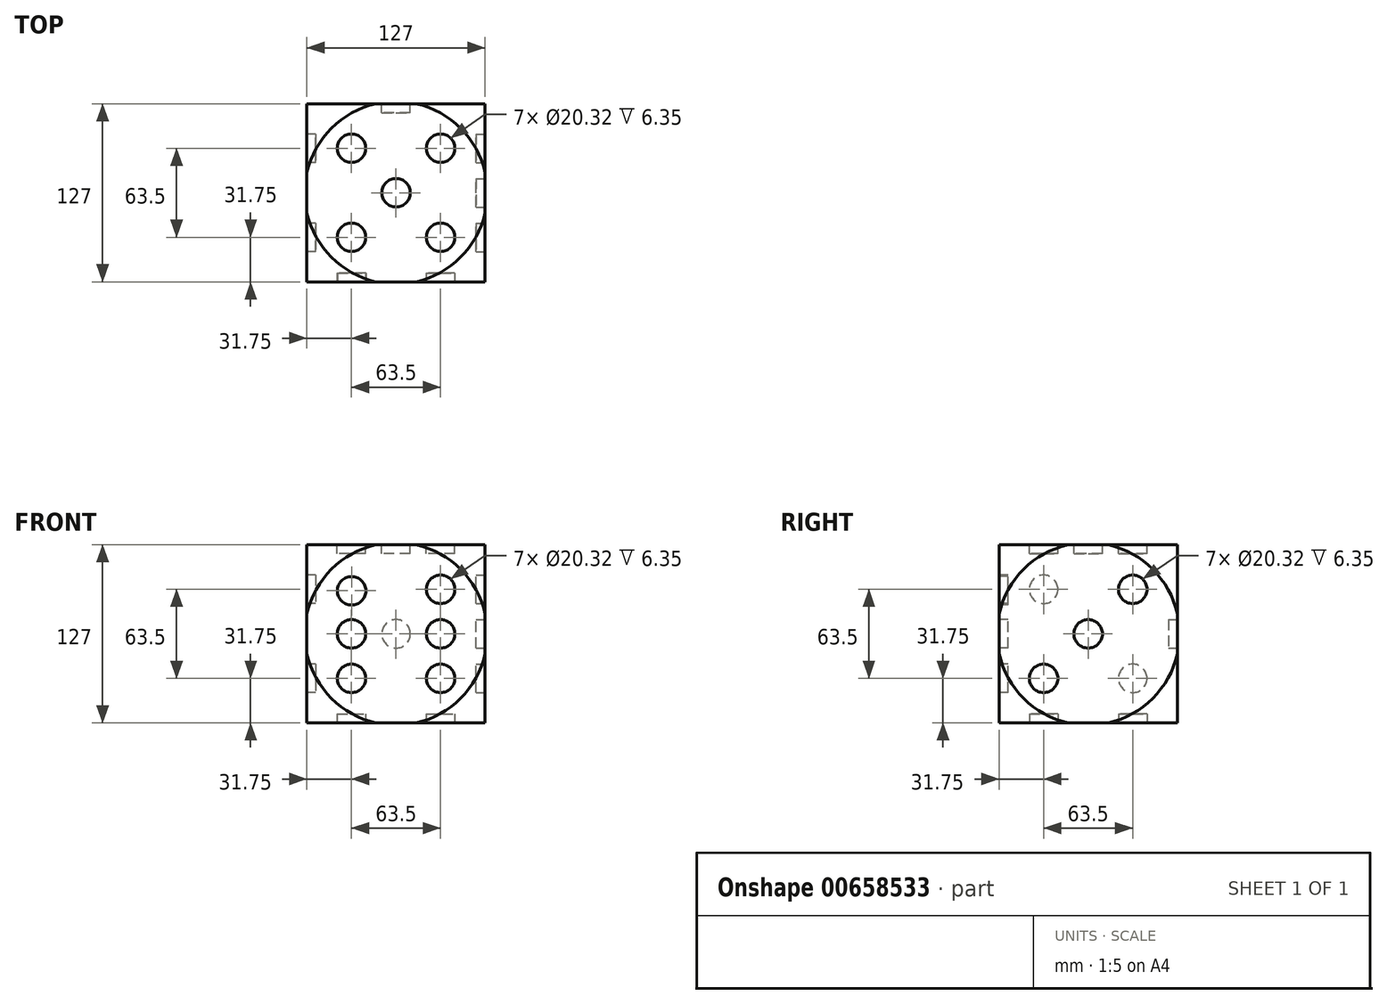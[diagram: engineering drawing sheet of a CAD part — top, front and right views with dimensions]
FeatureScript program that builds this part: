
annotation { "Feature Type Name" : "Feature", "Feature Type Description" : "" }
export const myFeature = defineFeature(function(context is Context, id is Id, definition is map)
    precondition{}
    {
        {
            var Q0;
            Q0=qCreatedBy(makeId("Top.planeOp"),FACE);
            var sketch = newSketch(context, id + "F0", { "sketchPlane" : qUnion([Q0])});
            skLineSegment(sketch, "E0.bottom", {"start": v(63.5, -63.5) * mm, "end": v(-63.5, -63.5) * mm});
            skLineSegment(sketch, "E0.top", {"start": v(63.5, 63.5) * mm, "end": v(-63.5, 63.5) * mm});
            skLineSegment(sketch, "E0.left", {"start": v(63.5, -63.5) * mm, "end": v(63.5, 63.5) * mm});
            skLineSegment(sketch, "E0.right", {"start": v(-63.5, -63.5) * mm, "end": v(-63.5, 63.5) * mm});
            skPoint(sketch, "E0.middle", {"position": v(0, 0) * mm});
            skSolve(sketch);
        }
        {
            var Q0;
            Q0=qCreatedBy(makeId("Top.planeOp"),FACE);
            cPlane(context, id + "F1", {"entities" : qUnion([Q0]), "cplaneType" : CPlaneType.OFFSET, "offset" : 63.5 * mm, "width" : 152.4 * mm, "height" : 152.4 * mm});
        }
        {
            var Q0;
            Q0 = qSketchRegion(id + "F0", true);
            extrude(context, id + "F2", {"entities" : qUnion([Q0]), "depth" : 127 * mm, "offsetDistance" : 25.4 * mm});
        }
        {
            var Q0;
            Q0=qCreatedBy(id+"F1.planeOp",FACE);
            var sketch = newSketch(context, id + "F3", { "sketchPlane" : qUnion([Q0])});
            skArc(sketch, "E1", {"start": v(0, 90.94) * mm, "mid": v(-90.94, 0) * mm, "end": v(0, -90.94) * mm});
            skLineSegment(sketch, "E2", {"start": v(0, 90.94) * mm, "end": v(0, -90.94) * mm});
            skSolve(sketch);
        }
        {
            var Q0;
            Q0 = qSketchRegion(id + "F3", true);
            var Q1;
            Q1=sQuery(id+"F3.wireOp",EDGE,"E2");
            revolve(context, id + "F4", {"entities" : qUnion([Q0]), "axis" : qUnion([Q1]), "revolveType" : RevolveType.FULL});
        }
        {
            var Q0;
            Q0=makeQuery(id+"F4.opRevolve","SWEPT_BODY",BODY,{"disambiguationData":[OSD([sQuery(id+"F3.wireOp",EDGE,"E1"),sQuery(id+"F3.wireOp",EDGE,"E2")])]});
            var Q1;
            Q1=makeQuery(id+"F2.opExtrude","SWEPT_BODY",BODY,{"disambiguationData":[OSD([sQuery(id+"F0.wireOp",EDGE,"E0.bottom"),sQuery(id+"F0.wireOp",EDGE,"E0.top"),sQuery(id+"F0.wireOp",EDGE,"E0.left"),sQuery(id+"F0.wireOp",EDGE,"E0.right")])]});
            booleanBodies(context, id + "F5", {"operationType" : BooleanOperationType.INTERSECTION, "tools" : qUnion([Q0, Q1])});
        }
        {
            var Q0;
            Q0=makeQuery(id+"F2.opExtrude","SWEPT_FACE",FACE,{"disambiguationData":[OSD([sQuery(id+"F0.wireOp",EDGE,"E0.top")])]});
            var sketch = newSketch(context, id + "F6", { "sketchPlane" : qUnion([Q0])});
            skCircle(sketch, "E3", {"center": v(0, 63.5) * mm, "radius": 10.16 * mm});
            skSolve(sketch);
        }
        {
            var Q0;
            Q0=makeQuery(id+"F6.imprint","IMPRINT",FACE,{"disambiguationData":[TD([[makeQuery(id+"F6.imprint","IMPRINT",EDGE,{"derivedFrom":sQuery(id+"F6.wireOp",EDGE,"E3")}),1.0]])]});
            var Q1;
            Q1=sQuery(id+"F6.wireOp",EDGE,"E3");
            extrude(context, id + "F7", {"entities" : qUnion([Q0]), "operationType" : NewBodyOperationType.REMOVE, "surfaceEntities" : qUnion([Q1]), "oppositeDirection" : true, "depth" : 6.35 * mm, "offsetDistance" : 25.4 * mm});
        }
        {
            var Q0;
            Q0=makeQuery(id+"F2.opExtrude","SWEPT_FACE",FACE,{"disambiguationData":[OSD([sQuery(id+"F0.wireOp",EDGE,"E0.bottom")])]});
            var sketch = newSketch(context, id + "F8", { "sketchPlane" : qUnion([Q0])});
            skLineSegment(sketch, "E4", {"start": v(0, 0) * mm, "end": v(0, 127) * mm, "construction": true});
            skLineSegment(sketch, "E5", {"start": v(0, 127) * mm, "end": v(0, 127) * mm});
            skLineSegment(sketch, "E6", {"start": v(-63.5, 63.5) * mm, "end": v(63.5, 63.5) * mm, "construction": true});
            skLineSegment(sketch, "E7", {"start": v(46.03, 109.53) * mm, "end": v(0, 63.5) * mm, "construction": true});
            skLineSegment(sketch, "E8", {"start": v(0, 63.5) * mm, "end": v(46.03, 17.47) * mm, "construction": true});
            skLineSegment(sketch, "E9", {"start": v(46.03, 17.47) * mm, "end": v(46.03, 17.47) * mm});
            skLineSegment(sketch, "E10", {"start": v(0, 63.5) * mm, "end": v(-46.03, 17.47) * mm, "construction": true});
            skLineSegment(sketch, "E11", {"start": v(0, 63.5) * mm, "end": v(-46.03, 109.53) * mm, "construction": true});
            skLineSegment(sketch, "E12", {"start": v(0, 63.5) * mm, "end": v(31.75, 63.5) * mm, "construction": true});
            skLineSegment(sketch, "E13", {"start": v(0, 63.5) * mm, "end": v(-31.75, 63.5) * mm, "construction": true});
            skLineSegment(sketch, "E14", {"start": v(-31.75, 63.5) * mm, "end": v(-31.75, 63.5) * mm});
            skLineSegment(sketch, "E15", {"start": v(31.75, 63.5) * mm, "end": v(31.75, 95.25) * mm, "construction": true});
            skLineSegment(sketch, "E16", {"start": v(31.75, 95.25) * mm, "end": v(31.75, 95.25) * mm});
            skLineSegment(sketch, "E17", {"start": v(31.75, 63.5) * mm, "end": v(31.75, 31.75) * mm, "construction": true});
            skLineSegment(sketch, "E18", {"start": v(-31.75, 63.5) * mm, "end": v(-31.75, 95.25) * mm, "construction": true});
            skLineSegment(sketch, "E19", {"start": v(-31.75, 63.5) * mm, "end": v(-31.75, 31.75) * mm, "construction": true});
            skCircle(sketch, "E20", {"center": v(31.75, 95.25) * mm, "radius": 10.16 * mm});
            skCircle(sketch, "E21", {"center": v(31.75, 63.5) * mm, "radius": 10.16 * mm});
            skCircle(sketch, "E22", {"center": v(31.75, 31.75) * mm, "radius": 10.16 * mm});
            skCircle(sketch, "E23", {"center": v(-31.75, 31.75) * mm, "radius": 10.16 * mm});
            skCircle(sketch, "E24", {"center": v(-31.75, 63.5) * mm, "radius": 10.16 * mm});
            skCircle(sketch, "E25", {"center": v(-31.64, 94.17) * mm, "radius": 10.16 * mm});
            skSolve(sketch);
        }
        {
            var Q0;
            Q0 = qSketchRegion(id + "F8", true);
            extrude(context, id + "F9", {"entities" : qUnion([Q0]), "operationType" : NewBodyOperationType.REMOVE, "oppositeDirection" : true, "depth" : 6.35 * mm, "offsetDistance" : 25.4 * mm});
        }
        {
            var Q0;
            Q0=makeQuery(id+"F2.opExtrude","CAP_FACE",FACE,{"disambiguationData":[OSD([sQuery(id+"F0.wireOp",EDGE,"E0.bottom"),sQuery(id+"F0.wireOp",EDGE,"E0.top"),sQuery(id+"F0.wireOp",EDGE,"E0.left"),sQuery(id+"F0.wireOp",EDGE,"E0.right")])],"isStart":false});
            var sketch = newSketch(context, id + "F10", { "sketchPlane" : qUnion([Q0])});
            skLineSegment(sketch, "E26", {"start": v(0, 63.5) * mm, "end": v(0, -63.5) * mm, "construction": true});
            skLineSegment(sketch, "E27", {"start": v(0, -63.5) * mm, "end": v(0, -63.5) * mm});
            skLineSegment(sketch, "E28", {"start": v(-63.5, 0) * mm, "end": v(-31.75, 0) * mm, "construction": true});
            skLineSegment(sketch, "E29", {"start": v(63.5, 0) * mm, "end": v(63.5, 0) * mm});
            skLineSegment(sketch, "E30", {"start": v(0, 0) * mm, "end": v(46.03, 46.03) * mm, "construction": true});
            skLineSegment(sketch, "E31", {"start": v(46.03, 46.03) * mm, "end": v(46.03, 46.03) * mm});
            skLineSegment(sketch, "E32", {"start": v(0, 0) * mm, "end": v(46.03, -46.03) * mm, "construction": true});
            skLineSegment(sketch, "E33", {"start": v(0, 0) * mm, "end": v(-46.03, -46.03) * mm, "construction": true});
            skLineSegment(sketch, "E34", {"start": v(0, 0) * mm, "end": v(-46.03, 46.03) * mm, "construction": true});
            skLineSegment(sketch, "E35", {"start": v(0, 0) * mm, "end": v(-31.75, 0) * mm, "construction": true});
            skLineSegment(sketch, "E36", {"start": v(31.75, 0) * mm, "end": v(31.75, 31.75) * mm, "construction": true});
            skLineSegment(sketch, "E37", {"start": v(31.75, 31.75) * mm, "end": v(31.75, 31.75) * mm});
            skLineSegment(sketch, "E38", {"start": v(-31.75, 0) * mm, "end": v(-31.75, -31.75) * mm, "construction": true});
            skLineSegment(sketch, "E39", {"start": v(-31.75, -31.75) * mm, "end": v(-31.75, -31.75) * mm});
            skLineSegment(sketch, "E40", {"start": v(-31.75, 0) * mm, "end": v(-31.75, 31.75) * mm, "construction": true});
            skLineSegment(sketch, "E41.trimOffspring", {"start": v(0, 0) * mm, "end": v(63.5, 0) * mm, "construction": true});
            skLineSegment(sketch, "E42", {"start": v(31.75, 0) * mm, "end": v(31.75, -31.75) * mm, "construction": true});
            skCircle(sketch, "E43", {"center": v(0, 0) * mm, "radius": 10.16 * mm});
            skCircle(sketch, "E44", {"center": v(31.75, 31.75) * mm, "radius": 10.16 * mm});
            skCircle(sketch, "E45", {"center": v(31.75, -31.75) * mm, "radius": 10.16 * mm});
            skCircle(sketch, "E46", {"center": v(-31.75, -31.75) * mm, "radius": 10.16 * mm});
            skCircle(sketch, "E47", {"center": v(-31.75, 31.75) * mm, "radius": 10.16 * mm});
            skSolve(sketch);
        }
        {
            var Q0;
            Q0 = qSketchRegion(id + "F10", true);
            extrude(context, id + "F11", {"entities" : qUnion([Q0]), "operationType" : NewBodyOperationType.REMOVE, "oppositeDirection" : true, "depth" : 6.35 * mm, "offsetDistance" : 25.4 * mm});
        }
        {
            var Q0;
            Q0=makeQuery(id+"F2.opExtrude","CAP_FACE",FACE,{"disambiguationData":[OSD([sQuery(id+"F0.wireOp",EDGE,"E0.bottom"),sQuery(id+"F0.wireOp",EDGE,"E0.top"),sQuery(id+"F0.wireOp",EDGE,"E0.left"),sQuery(id+"F0.wireOp",EDGE,"E0.right")])],"isStart":true});
            var sketch = newSketch(context, id + "F12", { "sketchPlane" : qUnion([Q0])});
            skLineSegment(sketch, "E48", {"start": v(0, 0) * mm, "end": v(63.5, 0) * mm, "construction": true});
            skLineSegment(sketch, "E49", {"start": v(63.5, 0) * mm, "end": v(63.5, 0) * mm});
            skLineSegment(sketch, "E50", {"start": v(0, 0) * mm, "end": v(-63.5, 0) * mm});
            skLineSegment(sketch, "E51", {"start": v(-63.5, 0) * mm, "end": v(0, 0) * mm, "construction": true});
            skLineSegment(sketch, "E52", {"start": v(0, 0) * mm, "end": v(-46.03, -46.03) * mm, "construction": true});
            skLineSegment(sketch, "E53", {"start": v(-46.03, -46.03) * mm, "end": v(-46.03, -46.03) * mm});
            skLineSegment(sketch, "E54", {"start": v(0, 0) * mm, "end": v(46.03, 46.03) * mm, "construction": true});
            skLineSegment(sketch, "E55", {"start": v(46.03, 46.03) * mm, "end": v(46.03, 46.03) * mm});
            skLineSegment(sketch, "E56", {"start": v(31.75, 0) * mm, "end": v(31.75, 31.75) * mm, "construction": true});
            skPoint(sketch, "E56.endSnap0", {"position": v(31.75, 0) * mm});
            skLineSegment(sketch, "E57", {"start": v(-31.75, 0) * mm, "end": v(-31.75, -31.75) * mm, "construction": true});
            skCircle(sketch, "E58", {"center": v(31.75, 31.75) * mm, "radius": 10.16 * mm});
            skCircle(sketch, "E59", {"center": v(-31.75, -31.75) * mm, "radius": 10.16 * mm});
            skSolve(sketch);
        }
        {
            var Q0;
            Q0 = qSketchRegion(id + "F12", true);
            extrude(context, id + "F13", {"entities" : qUnion([Q0]), "operationType" : NewBodyOperationType.REMOVE, "oppositeDirection" : true, "depth" : 6.35 * mm, "offsetDistance" : 25.4 * mm});
        }
        {
            var Q0;
            Q0=makeQuery(id+"F2.opExtrude","SWEPT_FACE",FACE,{"disambiguationData":[OSD([sQuery(id+"F0.wireOp",EDGE,"E0.left")])]});
            var sketch = newSketch(context, id + "F14", { "sketchPlane" : qUnion([Q0])});
            skLineSegment(sketch, "E60", {"start": v(0, 63.5) * mm, "end": v(63.5, 63.5) * mm, "construction": true});
            skLineSegment(sketch, "E61", {"start": v(0, 63.5) * mm, "end": v(-63.5, 63.5) * mm, "construction": true});
            skLineSegment(sketch, "E62", {"start": v(0, 63.5) * mm, "end": v(46.03, 109.53) * mm, "construction": true});
            skLineSegment(sketch, "E63", {"start": v(0, 63.5) * mm, "end": v(-46.03, 17.47) * mm, "construction": true});
            skLineSegment(sketch, "E64", {"start": v(-46.03, 17.47) * mm, "end": v(-46.03, 17.47) * mm});
            skLineSegment(sketch, "E65", {"start": v(31.75, 63.5) * mm, "end": v(31.75, 95.25) * mm});
            skLineSegment(sketch, "E66", {"start": v(-31.75, 63.5) * mm, "end": v(-31.75, 31.75) * mm});
            skCircle(sketch, "E67", {"center": v(0, 63.5) * mm, "radius": 10.16 * mm});
            skCircle(sketch, "E68", {"center": v(31.75, 95.25) * mm, "radius": 10.16 * mm});
            skCircle(sketch, "E69", {"center": v(-31.75, 31.75) * mm, "radius": 10.16 * mm});
            skSolve(sketch);
        }
        {
            var Q0;
            Q0 = qSketchRegion(id + "F14", true);
            extrude(context, id + "F15", {"entities" : qUnion([Q0]), "operationType" : NewBodyOperationType.REMOVE, "oppositeDirection" : true, "depth" : 6.35 * mm, "offsetDistance" : 25.4 * mm});
        }
        {
            var Q0;
            Q0=makeQuery(id+"F2.opExtrude","SWEPT_FACE",FACE,{"disambiguationData":[OSD([sQuery(id+"F0.wireOp",EDGE,"E0.right")])]});
            var sketch = newSketch(context, id + "F16", { "sketchPlane" : qUnion([Q0])});
            skLineSegment(sketch, "E70", {"start": v(0, 63.5) * mm, "end": v(63.5, 63.5) * mm, "construction": true});
            skLineSegment(sketch, "E71", {"start": v(63.5, 63.5) * mm, "end": v(63.5, 63.5) * mm});
            skLineSegment(sketch, "E72", {"start": v(0, 63.5) * mm, "end": v(-63.5, 63.5) * mm, "construction": true});
            skLineSegment(sketch, "E73", {"start": v(0, 63.5) * mm, "end": v(46.03, 109.53) * mm, "construction": true});
            skLineSegment(sketch, "E74", {"start": v(0, 63.5) * mm, "end": v(-46.03, 17.47) * mm, "construction": true});
            skLineSegment(sketch, "E75", {"start": v(-31.75, 63.5) * mm, "end": v(-31.75, 31.75) * mm, "construction": true});
            skLineSegment(sketch, "E76", {"start": v(-31.75, 31.75) * mm, "end": v(-31.75, 31.75) * mm});
            skLineSegment(sketch, "E77", {"start": v(0, 63.5) * mm, "end": v(-46.03, 109.53) * mm, "construction": true});
            skLineSegment(sketch, "E78", {"start": v(-46.03, 109.53) * mm, "end": v(-46.03, 109.53) * mm});
            skLineSegment(sketch, "E79", {"start": v(0, 63.5) * mm, "end": v(46.03, 17.47) * mm, "construction": true});
            skLineSegment(sketch, "E80", {"start": v(-31.75, 63.5) * mm, "end": v(-31.75, 95.25) * mm, "construction": true});
            skLineSegment(sketch, "E81", {"start": v(31.75, 63.5) * mm, "end": v(31.75, 95.25) * mm, "construction": true});
            skLineSegment(sketch, "E82", {"start": v(31.75, 63.5) * mm, "end": v(31.75, 31.75) * mm, "construction": true});
            skCircle(sketch, "E83", {"center": v(-31.75, 95.25) * mm, "radius": 10.16 * mm});
            skCircle(sketch, "E84", {"center": v(-31.75, 31.75) * mm, "radius": 10.16 * mm});
            skCircle(sketch, "E85", {"center": v(31.75, 31.75) * mm, "radius": 10.16 * mm});
            skCircle(sketch, "E86", {"center": v(31.75, 95.25) * mm, "radius": 10.16 * mm});
            skSolve(sketch);
        }
        {
            var Q0;
            Q0 = qSketchRegion(id + "F16", true);
            extrude(context, id + "F17", {"entities" : qUnion([Q0]), "operationType" : NewBodyOperationType.REMOVE, "oppositeDirection" : true, "depth" : 6.35 * mm, "offsetDistance" : 25.4 * mm});
        }
    });
